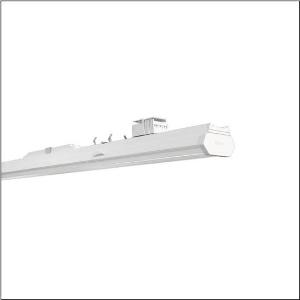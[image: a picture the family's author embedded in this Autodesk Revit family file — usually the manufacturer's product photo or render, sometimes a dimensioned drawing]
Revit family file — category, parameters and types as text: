
# Revit family: licross_r__11_protected_ho_51tp11mn4gxs_ec8e
name_source: partatom
category: Lighting Fixtures
units: mm (PartAtom-declared; Revit-internal decimal feet)

## family parameters
Cut with Voids When Loaded = No
Host = Face
Light Source = No
Part Type = Normal
Room Calculation Point = No
Round Connector Dimension = Use Diameter
Shared = No

## types (1)
- --- (1 x LED, 16070 lm, 87.4 W, 4000K)
    Apparent Load = 87 VA
    CIE Flux Codes = 84 94 98 99 100
    Color Rendering = 80
    Color Temperature = 4000K
    Default Elevation = 1800 mm
    Description = Licross® 11 Protected HO, luminaire insert, of sheet steel, galvanised, coil coated, white, length: 1.500mm, width: 90mm, height: 101mm, LED rated luminous flux: 16.070lm, light colour: 840, control gear: ON/OFF Multilumen, with plug, 3-pole, with phase selection, mains connection: 220..240V, AC, 50/60Hz, rated input power: 87W, halogen-free wiring, primary light control with lens, of plastic, primary optical cover: cover, of PMMA, light emission: direct distribution, primary light characteristic: symmetric, protection rating (complete): IP64, insulation class (complete): insulation class I (protective earthing), certification: CE, ENEC, VDE, UKCA, protection symbol: D if used in an environment with conductive dust loads with corresponding accessories, impact resistance: IK06, permissible ambient temperature for indoor applications: -35..+35°C, corresponds to IFS (International Featured Standards) requirements for safety and quality in the food industry, reducing of maximum allowable ambient temperature of 5°C with ceiling mounting, LABS conformity tested according to VDMA 24364:2018-05, packaging unit: 1 piece
    Height = 92 mm
    Lamp = 1 x LED
    Lamp Light Flux = 16070 lm
    Lamp Power = 87.4 W
    Lamp count = 1
    Length = 1500 mm
    Luminous efficacy = 184 lm/W
    Manufacturer = Siteco
    ModVariant = No
    Model = 51TP11MN4GXS
    Mounting Place = Ceiling
    Mounting Type = Pendant
    Number of Poles = 1
    OnlyDefault = Yes
    Power Factor = 1
    Product Name = Licross® 11 Protected HO
    Product group = luminaire insert
    ProductGroupID = 901
    Protection Class = Protection class I
    Protection Degree = IP 64
    RLX_Detail_Level = 1
    RLX_Emergency_Light_Flux = 0 lm
    RLX_Emergency_Type = 0
    RLX_Emergency_Type_DB = No
    RlxData = <blob elided: 21993 chars, md5=56c626c5>
    Socket = socket
    Standby Power = 0 W
    System Light Flux = 16070 lm
    System Power = 87 W
    Type Comments = factory setting: luminous flux: 100 % | (A | C | E) | 203 mA
    Type Image = l_1256148.jpg
    URL = http://relux.com
    VarID = @adj_038041
    Voltage = 0 V
    Weight = 0.00 kg
    Width = 88 mm

## geometry (parser evidence)
native form markers: Blend x4, Sweep x13
no freeform markers — native parametric forms only
